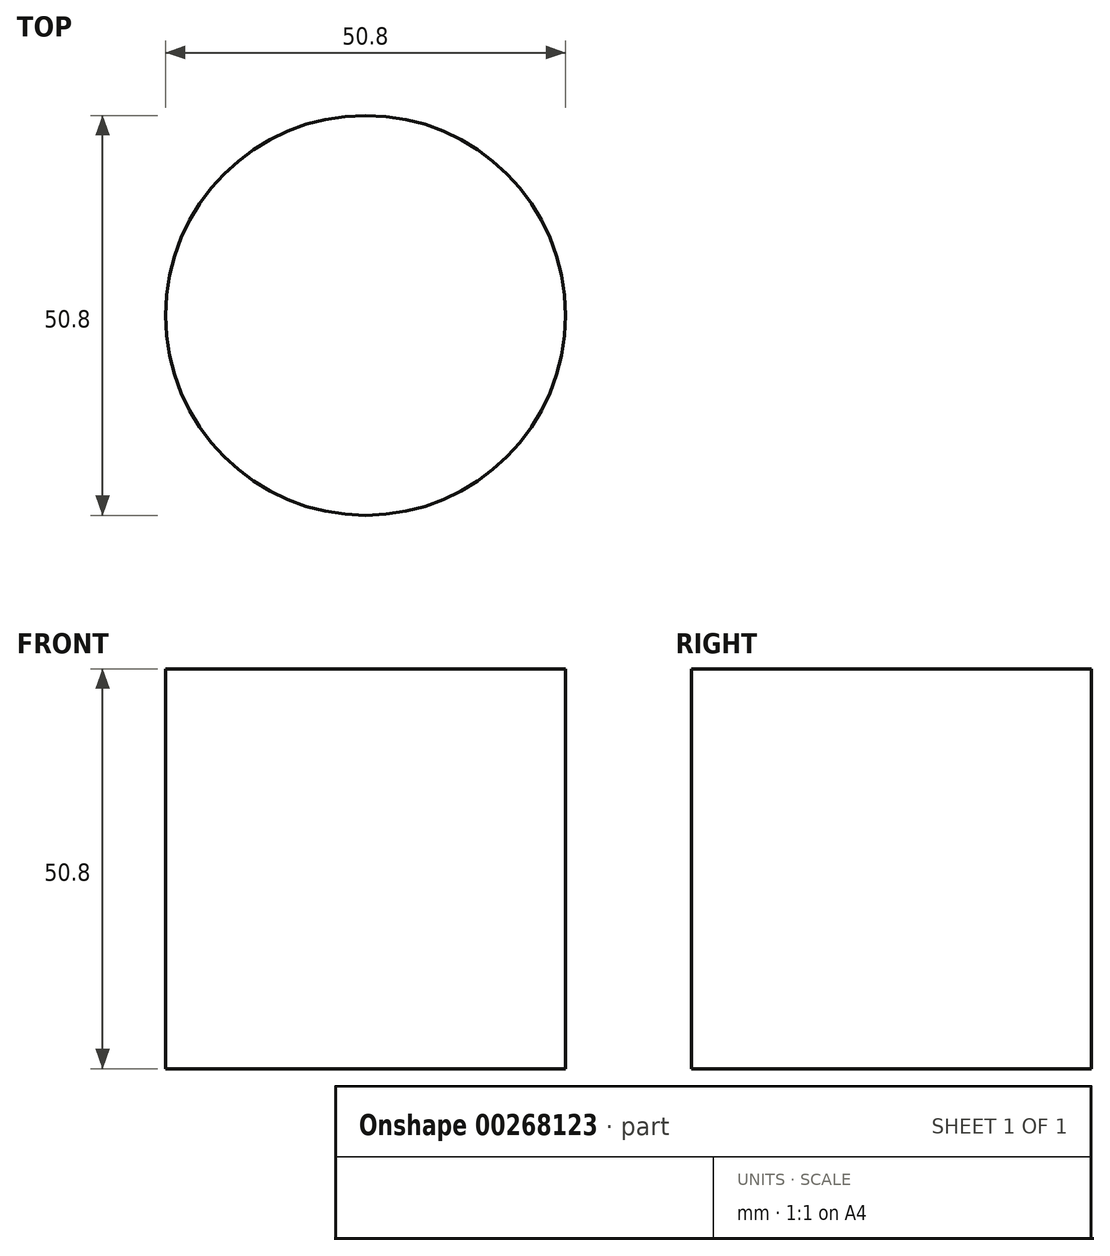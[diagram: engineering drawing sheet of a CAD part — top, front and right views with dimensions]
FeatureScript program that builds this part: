
annotation { "Feature Type Name" : "Feature", "Feature Type Description" : "" }
export const myFeature = defineFeature(function(context is Context, id is Id, definition is map)
    precondition{}
    {
        {
            var Q0;
            Q0=qCreatedBy(makeId("Front.planeOp"),FACE);
            var sketch = newSketch(context, id + "F0", { "sketchPlane" : qUnion([Q0])});
            skLineSegment(sketch, "E0.bottom", {"start": v(0, 0) * mm, "end": v(25.4, 0) * mm});
            skLineSegment(sketch, "E0.top", {"start": v(0, 50.8) * mm, "end": v(25.4, 50.8) * mm});
            skLineSegment(sketch, "E0.left", {"start": v(0, 0) * mm, "end": v(0, 50.8) * mm});
            skLineSegment(sketch, "E0.right", {"start": v(25.4, 0) * mm, "end": v(25.4, 50.8) * mm});
            skSolve(sketch);
        }
        {
            var Q0;
            Q0 = qSketchRegion(id + "F0", true);
            var Q1;
            Q1=sQuery(id+"F0.wireOp",EDGE,"E0.left");
            revolve(context, id + "F1", {"entities" : qUnion([Q0]), "axis" : qUnion([Q1]), "revolveType" : RevolveType.FULL});
        }
    });
